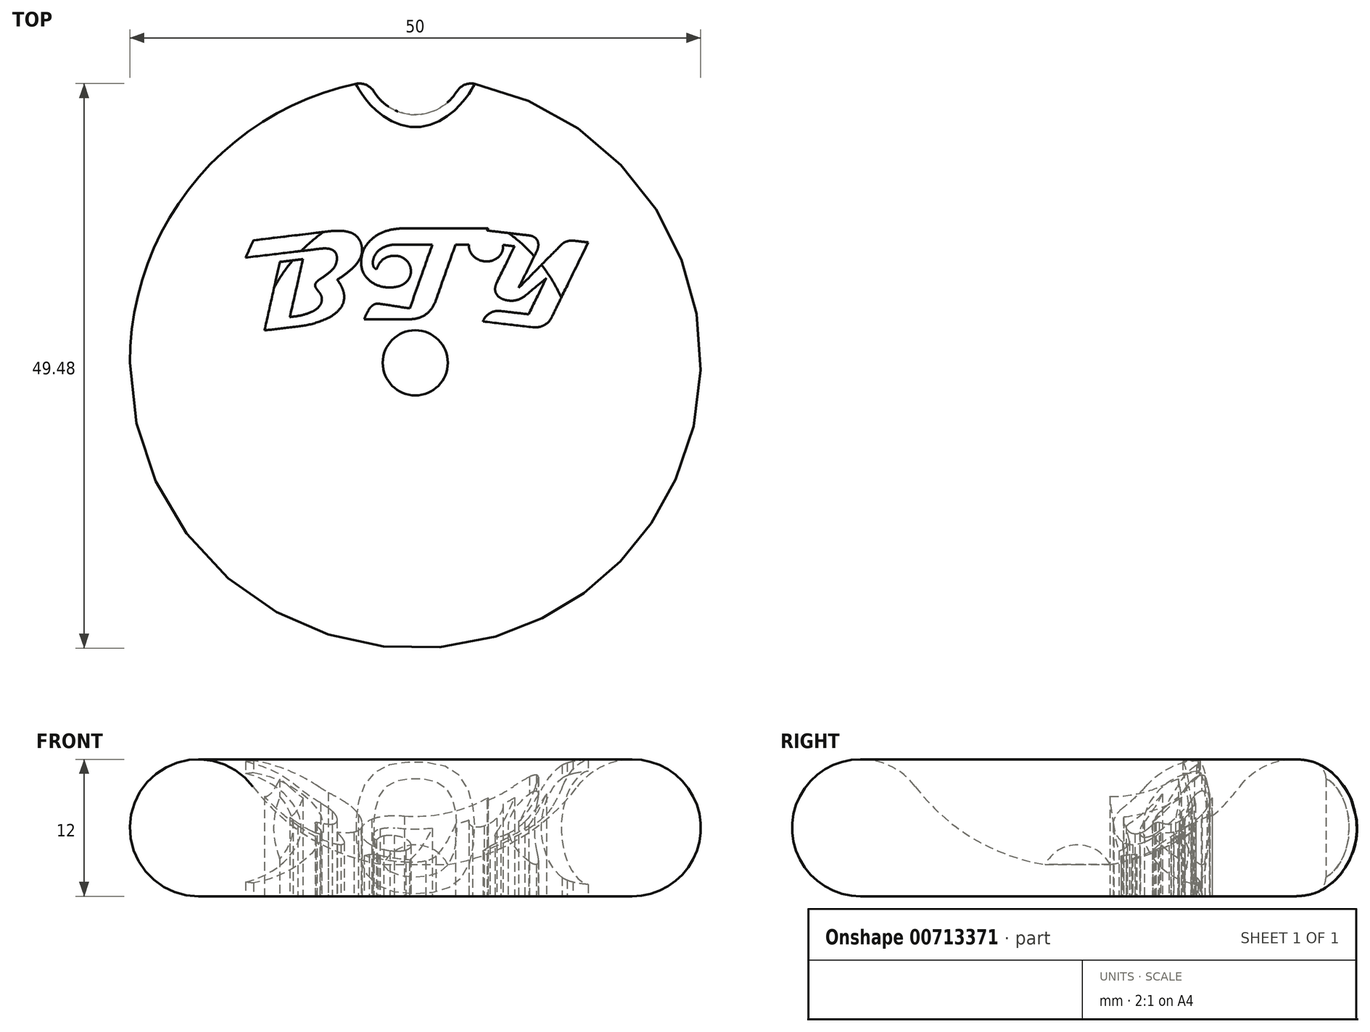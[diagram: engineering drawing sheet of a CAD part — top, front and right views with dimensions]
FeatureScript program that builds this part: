
annotation { "Feature Type Name" : "Feature", "Feature Type Description" : "" }
export const myFeature = defineFeature(function(context is Context, id is Id, definition is map)
    precondition{}
    {
        {
            var Q0;
            Q0=qCreatedBy(makeId("Front.planeOp"),FACE);
            var sketch = newSketch(context, id + "F0", { "sketchPlane" : qUnion([Q0])});
            skArc(sketch, "E0", {"start": v(-14.21, 9.62) * mm, "mid": v(-24.37, 8.67) * mm, "end": v(-19, 0) * mm});
            skArc(sketch, "E1", {"start": v(-14.21, 9.62) * mm, "mid": v(-9.2, 5.1) * mm, "end": v(-2.85, 2.78) * mm});
            skLineSegment(sketch, "E2", {"start": v(-19, 0) * mm, "end": v(0, 0) * mm});
            skLineSegment(sketch, "E3", {"start": v(0, 0) * mm, "end": v(0, 2.55) * mm});
            skLineSegment(sketch, "E4", {"start": v(0, 2.55) * mm, "end": v(0, 4.5) * mm});
            skArc(sketch, "E5", {"start": v(0, 4.5) * mm, "mid": v(-1.67, 4.04) * mm, "end": v(-2.85, 2.78) * mm});
            skSolve(sketch);
        }
        {
            var Q0;
            Q0=makeQuery(id+"F0.imprint","IMPRINT",FACE,{"disambiguationData":[TD([[makeQuery(id+"F0.imprint","IMPRINT",EDGE,{"derivedFrom":sQuery(id+"F0.wireOp",EDGE,"E0")}),1.0]])]});
            var Q1;
            Q1=sQuery(id+"F0.wireOp",EDGE,"E3");
            revolve(context, id + "F1", {"surfaceOperationType" : NewSurfaceOperationType.NEW, "entities" : qUnion([Q0]), "axis" : qUnion([Q1]), "revolveType" : RevolveType.FULL});
        }
        {
            var Q0;
            Q0=qCreatedBy(makeId("Top.planeOp"),FACE);
            var sketch = newSketch(context, id + "F2", { "sketchPlane" : qUnion([Q0])});
            skArc(sketch, "E6", {"start": v(4.7, 10.37) * mm, "mid": v(4.76, 9.86) * mm, "end": v(5.03, 9.42) * mm});
            skArc(sketch, "E7", {"start": v(5.03, 9.42) * mm, "mid": v(5.49, 9.06) * mm, "end": v(6.04, 8.9) * mm});
            skArc(sketch, "E8", {"start": v(6.04, 8.9) * mm, "mid": v(6.62, 8.93) * mm, "end": v(7.14, 9.17) * mm});
            skArc(sketch, "E9", {"start": v(7.14, 9.17) * mm, "mid": v(7.51, 9.56) * mm, "end": v(7.69, 10.07) * mm});
            skArc(sketch, "E10", {"start": v(7.69, 10.07) * mm, "mid": v(7.7, 10.2) * mm, "end": v(7.7, 10.33) * mm});
            skLineSegment(sketch, "E11", {"start": v(7.7, 10.33) * mm, "end": v(8.7, 10.21) * mm});
            skLineSegment(sketch, "E12", {"start": v(8.7, 10.21) * mm, "end": v(7.13, 7.03) * mm});
            skArc(sketch, "E13", {"start": v(7.13, 7.03) * mm, "mid": v(7.05, 6.81) * mm, "end": v(7, 6.58) * mm});
            skArc(sketch, "E14", {"start": v(7, 6.58) * mm, "mid": v(7.05, 6.15) * mm, "end": v(7.31, 5.8) * mm});
            skArc(sketch, "E15", {"start": v(7.31, 5.8) * mm, "mid": v(7.7, 5.57) * mm, "end": v(8.14, 5.47) * mm});
            skArc(sketch, "E16", {"start": v(8.14, 5.47) * mm, "mid": v(8.9, 5.5) * mm, "end": v(9.6, 5.86) * mm});
            skLineSegment(sketch, "E17", {"start": v(9.6, 5.86) * mm, "end": v(11.5, 7.45) * mm});
            skLineSegment(sketch, "E18", {"start": v(11.5, 7.45) * mm, "end": v(9.92, 4.26) * mm});
            skLineSegment(sketch, "E19", {"start": v(9.92, 4.26) * mm, "end": v(7.5, 4.54) * mm});
            skArc(sketch, "E20", {"start": v(7.5, 4.54) * mm, "mid": v(7, 4.53) * mm, "end": v(6.54, 4.36) * mm});
            skArc(sketch, "E21", {"start": v(6.54, 4.36) * mm, "mid": v(6.17, 4.05) * mm, "end": v(5.93, 3.63) * mm});
            skLineSegment(sketch, "E22", {"start": v(5.93, 3.63) * mm, "end": v(10.28, 3.12) * mm});
            skArc(sketch, "E23", {"start": v(10.28, 3.12) * mm, "mid": v(10.78, 3.13) * mm, "end": v(11.26, 3.3) * mm});
            skArc(sketch, "E24", {"start": v(11.26, 3.3) * mm, "mid": v(11.66, 3.59) * mm, "end": v(11.95, 4) * mm});
            skLineSegment(sketch, "E25", {"start": v(11.95, 4) * mm, "end": v(15.14, 10.56) * mm});
            skLineSegment(sketch, "E26", {"start": v(15.14, 10.56) * mm, "end": v(13.82, 10.71) * mm});
            skArc(sketch, "E27", {"start": v(13.82, 10.71) * mm, "mid": v(13.55, 10.7) * mm, "end": v(13.3, 10.65) * mm});
            skArc(sketch, "E28", {"start": v(13.3, 10.65) * mm, "mid": v(13.06, 10.56) * mm, "end": v(12.85, 10.4) * mm});
            skLineSegment(sketch, "E29", {"start": v(12.85, 10.4) * mm, "end": v(9.05, 6.56) * mm});
            skLineSegment(sketch, "E30", {"start": v(9.05, 6.56) * mm, "end": v(10.64, 9.78) * mm});
            skArc(sketch, "E31", {"start": v(10.64, 9.78) * mm, "mid": v(10.72, 10) * mm, "end": v(10.77, 10.22) * mm});
            skArc(sketch, "E32", {"start": v(10.77, 10.22) * mm, "mid": v(10.75, 10.56) * mm, "end": v(10.6, 10.86) * mm});
            skArc(sketch, "E33", {"start": v(10.6, 10.86) * mm, "mid": v(10.33, 11.07) * mm, "end": v(10, 11.16) * mm});
            skLineSegment(sketch, "E34", {"start": v(10, 11.16) * mm, "end": v(6.35, 11.6) * mm});
            skLineSegment(sketch, "E35", {"start": v(6.35, 11.6) * mm, "end": v(6.28, 11.6) * mm});
            skLineSegment(sketch, "E36", {"start": v(6.28, 11.6) * mm, "end": v(6.39, 11.8) * mm});
            skLineSegment(sketch, "E37", {"start": v(6.39, 11.8) * mm, "end": v(-0.94, 11.79) * mm});
            skArc(sketch, "E38", {"start": v(-0.94, 11.79) * mm, "mid": v(-1.76, 11.73) * mm, "end": v(-2.57, 11.55) * mm});
            skArc(sketch, "E39", {"start": v(-2.57, 11.55) * mm, "mid": v(-3.23, 11.26) * mm, "end": v(-3.8, 10.84) * mm});
            skArc(sketch, "E40", {"start": v(-3.8, 10.84) * mm, "mid": v(-4.5, 9.95) * mm, "end": v(-4.74, 8.85) * mm});
            skArc(sketch, "E41", {"start": v(-4.74, 8.85) * mm, "mid": v(-4.54, 7.9) * mm, "end": v(-3.93, 7.15) * mm});
            skArc(sketch, "E42", {"start": v(-3.93, 7.15) * mm, "mid": v(-3.13, 6.74) * mm, "end": v(-2.24, 6.6) * mm});
            skArc(sketch, "E43", {"start": v(-2.24, 6.6) * mm, "mid": v(-1.83, 6.63) * mm, "end": v(-1.43, 6.72) * mm});
            skArc(sketch, "E44", {"start": v(-1.43, 6.72) * mm, "mid": v(-1.11, 6.85) * mm, "end": v(-0.83, 7.05) * mm});
            skArc(sketch, "E45", {"start": v(-0.83, 7.05) * mm, "mid": v(-0.5, 7.48) * mm, "end": v(-0.38, 8.02) * mm});
            skArc(sketch, "E46", {"start": v(-0.38, 8.02) * mm, "mid": v(-0.48, 8.53) * mm, "end": v(-0.76, 8.96) * mm});
            skArc(sketch, "E47", {"start": v(-0.76, 8.96) * mm, "mid": v(-1.25, 9.29) * mm, "end": v(-1.83, 9.39) * mm});
            skArc(sketch, "E48", {"start": v(-1.83, 9.39) * mm, "mid": v(-2.32, 9.32) * mm, "end": v(-2.77, 9.1) * mm});
            skArc(sketch, "E49", {"start": v(-2.77, 9.1) * mm, "mid": v(-3.15, 8.71) * mm, "end": v(-3.38, 8.21) * mm});
            skArc(sketch, "E50", {"start": v(-3.38, 8.21) * mm, "mid": v(-3.52, 8.27) * mm, "end": v(-3.63, 8.38) * mm});
            skArc(sketch, "E51", {"start": v(-3.63, 8.38) * mm, "mid": v(-3.7, 8.57) * mm, "end": v(-3.71, 8.77) * mm});
            skArc(sketch, "E52", {"start": v(-3.71, 8.77) * mm, "mid": v(-3.54, 9.43) * mm, "end": v(-3.08, 9.93) * mm});
            skArc(sketch, "E53", {"start": v(-3.08, 9.93) * mm, "mid": v(-2.46, 10.25) * mm, "end": v(-1.78, 10.36) * mm});
            skLineSegment(sketch, "E54", {"start": v(-1.78, 10.36) * mm, "end": v(1.5, 10.36) * mm});
            skLineSegment(sketch, "E55", {"start": v(1.5, 10.36) * mm, "end": v(-0.48, 4.77) * mm});
            skLineSegment(sketch, "E56", {"start": v(-0.48, 4.77) * mm, "end": v(-3.12, 5.18) * mm});
            skLineSegment(sketch, "E57", {"start": v(-3.12, 5.18) * mm, "end": v(-3.26, 5.2) * mm});
            skArc(sketch, "E58", {"start": v(-3.26, 5.2) * mm, "mid": v(-3.48, 5.16) * mm, "end": v(-3.68, 5.07) * mm});
            skArc(sketch, "E59", {"start": v(-3.68, 5.07) * mm, "mid": v(-3.87, 4.92) * mm, "end": v(-4.03, 4.72) * mm});
            skArc(sketch, "E60", {"start": v(-4.03, 4.72) * mm, "mid": v(-4.27, 4.28) * mm, "end": v(-4.47, 3.82) * mm});
            skLineSegment(sketch, "E61", {"start": v(-4.47, 3.82) * mm, "end": v(-0.5, 3.83) * mm});
            skArc(sketch, "E62", {"start": v(-0.5, 3.83) * mm, "mid": v(0.25, 3.92) * mm, "end": v(0.93, 4.25) * mm});
            skArc(sketch, "E63", {"start": v(0.93, 4.25) * mm, "mid": v(1.47, 4.81) * mm, "end": v(1.8, 5.51) * mm});
            skLineSegment(sketch, "E64", {"start": v(1.8, 5.51) * mm, "end": v(3.53, 10.37) * mm});
            skLineSegment(sketch, "E65", {"start": v(3.53, 10.37) * mm, "end": v(4.7, 10.37) * mm});
            skArc(sketch, "E66", {"start": v(-4.67, 10.08) * mm, "mid": v(-4.77, 10.5) * mm, "end": v(-4.97, 10.9) * mm});
            skArc(sketch, "E67", {"start": v(-4.97, 10.9) * mm, "mid": v(-5.27, 11.2) * mm, "end": v(-5.63, 11.4) * mm});
            skArc(sketch, "E68", {"start": v(-5.63, 11.4) * mm, "mid": v(-6.04, 11.52) * mm, "end": v(-6.47, 11.57) * mm});
            skArc(sketch, "E69", {"start": v(-6.47, 11.57) * mm, "mid": v(-7.04, 11.57) * mm, "end": v(-7.61, 11.52) * mm});
            skLineSegment(sketch, "E70", {"start": v(-7.61, 11.52) * mm, "end": v(-14.17, 10.74) * mm});
            skLineSegment(sketch, "E71", {"start": v(-14.17, 10.74) * mm, "end": v(-14.86, 9.22) * mm});
            skLineSegment(sketch, "E72", {"start": v(-14.86, 9.22) * mm, "end": v(-8.3, 10) * mm});
            skArc(sketch, "E73", {"start": v(-8.3, 10) * mm, "mid": v(-8, 10.03) * mm, "end": v(-7.7, 10.02) * mm});
            skArc(sketch, "E74", {"start": v(-7.7, 10.02) * mm, "mid": v(-7.49, 9.98) * mm, "end": v(-7.28, 9.9) * mm});
            skArc(sketch, "E75", {"start": v(-7.28, 9.9) * mm, "mid": v(-6.99, 9.66) * mm, "end": v(-6.87, 9.3) * mm});
            skArc(sketch, "E76", {"start": v(-6.87, 9.3) * mm, "mid": v(-6.94, 8.68) * mm, "end": v(-7.28, 8.15) * mm});
            skArc(sketch, "E77", {"start": v(-7.28, 8.15) * mm, "mid": v(-7.72, 7.76) * mm, "end": v(-8.22, 7.42) * mm});
            skArc(sketch, "E78", {"start": v(-8.22, 7.42) * mm, "mid": v(-8.41, 7.29) * mm, "end": v(-8.6, 7.13) * mm});
            skArc(sketch, "E79", {"start": v(-8.6, 7.13) * mm, "mid": v(-8.7, 7.01) * mm, "end": v(-8.77, 6.87) * mm});
            skArc(sketch, "E80", {"start": v(-8.77, 6.87) * mm, "mid": v(-8.77, 6.8) * mm, "end": v(-8.77, 6.75) * mm});
            skArc(sketch, "E81", {"start": v(-8.77, 6.75) * mm, "mid": v(-8.74, 6.65) * mm, "end": v(-8.69, 6.55) * mm});
            skArc(sketch, "E82", {"start": v(-8.69, 6.55) * mm, "mid": v(-8.6, 6.41) * mm, "end": v(-8.49, 6.28) * mm});
            skArc(sketch, "E83", {"start": v(-8.49, 6.28) * mm, "mid": v(-8.37, 6.13) * mm, "end": v(-8.28, 5.97) * mm});
            skArc(sketch, "E84", {"start": v(-8.28, 5.97) * mm, "mid": v(-8.22, 5.85) * mm, "end": v(-8.2, 5.7) * mm});
            skArc(sketch, "E85", {"start": v(-8.2, 5.7) * mm, "mid": v(-8.2, 5.34) * mm, "end": v(-8.36, 5.01) * mm});
            skArc(sketch, "E86", {"start": v(-8.36, 5.01) * mm, "mid": v(-8.68, 4.7) * mm, "end": v(-9.06, 4.47) * mm});
            skArc(sketch, "E87", {"start": v(-9.06, 4.47) * mm, "mid": v(-9.86, 4.2) * mm, "end": v(-10.7, 4.05) * mm});
            skLineSegment(sketch, "E88", {"start": v(-10.7, 4.05) * mm, "end": v(-10.98, 4.02) * mm});
            skLineSegment(sketch, "E89", {"start": v(-10.98, 4.02) * mm, "end": v(-9.84, 9.08) * mm});
            skLineSegment(sketch, "E90", {"start": v(-9.84, 9.08) * mm, "end": v(-11.86, 8.84) * mm});
            skLineSegment(sketch, "E91", {"start": v(-11.86, 8.84) * mm, "end": v(-13.2, 2.84) * mm});
            skLineSegment(sketch, "E92", {"start": v(-13.2, 2.84) * mm, "end": v(-10.28, 3.19) * mm});
            skArc(sketch, "E93", {"start": v(-10.28, 3.19) * mm, "mid": v(-8.93, 3.44) * mm, "end": v(-7.64, 3.94) * mm});
            skArc(sketch, "E94", {"start": v(-7.64, 3.94) * mm, "mid": v(-7.02, 4.32) * mm, "end": v(-6.51, 4.84) * mm});
            skArc(sketch, "E95", {"start": v(-6.51, 4.84) * mm, "mid": v(-6.27, 5.39) * mm, "end": v(-6.24, 5.98) * mm});
            skArc(sketch, "E96", {"start": v(-6.24, 5.98) * mm, "mid": v(-6.3, 6.3) * mm, "end": v(-6.42, 6.61) * mm});
            skArc(sketch, "E97", {"start": v(-6.42, 6.61) * mm, "mid": v(-6.61, 6.96) * mm, "end": v(-6.83, 7.28) * mm});
            skArc(sketch, "E98", {"start": v(-6.83, 7.28) * mm, "mid": v(-6.06, 7.81) * mm, "end": v(-5.36, 8.43) * mm});
            skArc(sketch, "E99", {"start": v(-5.36, 8.43) * mm, "mid": v(-5.04, 8.81) * mm, "end": v(-4.8, 9.25) * mm});
            skArc(sketch, "E100", {"start": v(-4.8, 9.25) * mm, "mid": v(-4.68, 9.66) * mm, "end": v(-4.67, 10.08) * mm});
            skSolve(sketch);
        }
        {
            var Q0;
            Q0 = qSketchRegion(id + "F2", true);
            extrude(context, id + "F3", {"entities" : qUnion([Q0]), "operationType" : NewBodyOperationType.REMOVE, "depth" : 50.8 * mm, "offsetDistance" : 25.4 * mm});
        }
        {
            var Q0;
            Q0=qCreatedBy(makeId("Front.planeOp"),FACE);
            var sketch = newSketch(context, id + "F4", { "sketchPlane" : qUnion([Q0])});
            skCircle(sketch, "E101", {"center": v(-19, 6) * mm, "radius": 5 * mm});
            skSolve(sketch);
        }
        {
            var Q0;
            Q0 = qSketchRegion(id + "F4", true);
            var Q1;
            Q1=sQuery(id+"F0.wireOp",EDGE,"E4");
            revolve(context, id + "F5", {"operationType" : NewBodyOperationType.ADD, "surfaceOperationType" : NewSurfaceOperationType.NEW, "entities" : qUnion([Q0]), "axis" : qUnion([Q1]), "revolveType" : RevolveType.FULL});
        }
        {
            var Q0;
            Q0=qCreatedBy(makeId("Top.planeOp"),FACE);
            var sketch = newSketch(context, id + "F6", { "sketchPlane" : qUnion([Q0])});
            skCircle(sketch, "E102", {"center": v(0, 26) * mm, "radius": 4.25 * mm});
            skSolve(sketch);
        }
        {
            var Q0;
            Q0 = qSketchRegion(id + "F6", true);
            extrude(context, id + "F7", {"entities" : qUnion([Q0]), "operationType" : NewBodyOperationType.REMOVE, "depth" : 25.4 * mm, "offsetDistance" : 25.4 * mm});
        }
        {
            var Q0;
            Q0=makeQuery(id+"F7.boolean.opBoolean","INTERSECT",EDGE,{"derivedFrom":[makeQuery(id+"F1.opRevolve","SWEPT_FACE",FACE,{"disambiguationData":[OSD([sQuery(id+"F0.wireOp",EDGE,"E0")])]}),makeQuery(id+"F7.opExtrude","SWEPT_FACE",FACE,{"disambiguationData":[OSD([sQuery(id+"F6.wireOp",EDGE,"E102")])]})]});
            fillet(context, id + "F8", {"entities" : qUnion([Q0]), "radius" : 1.5 * mm, "tangentPropagation" : true, "allowEdgeOverflow" : false});
        }
    });
